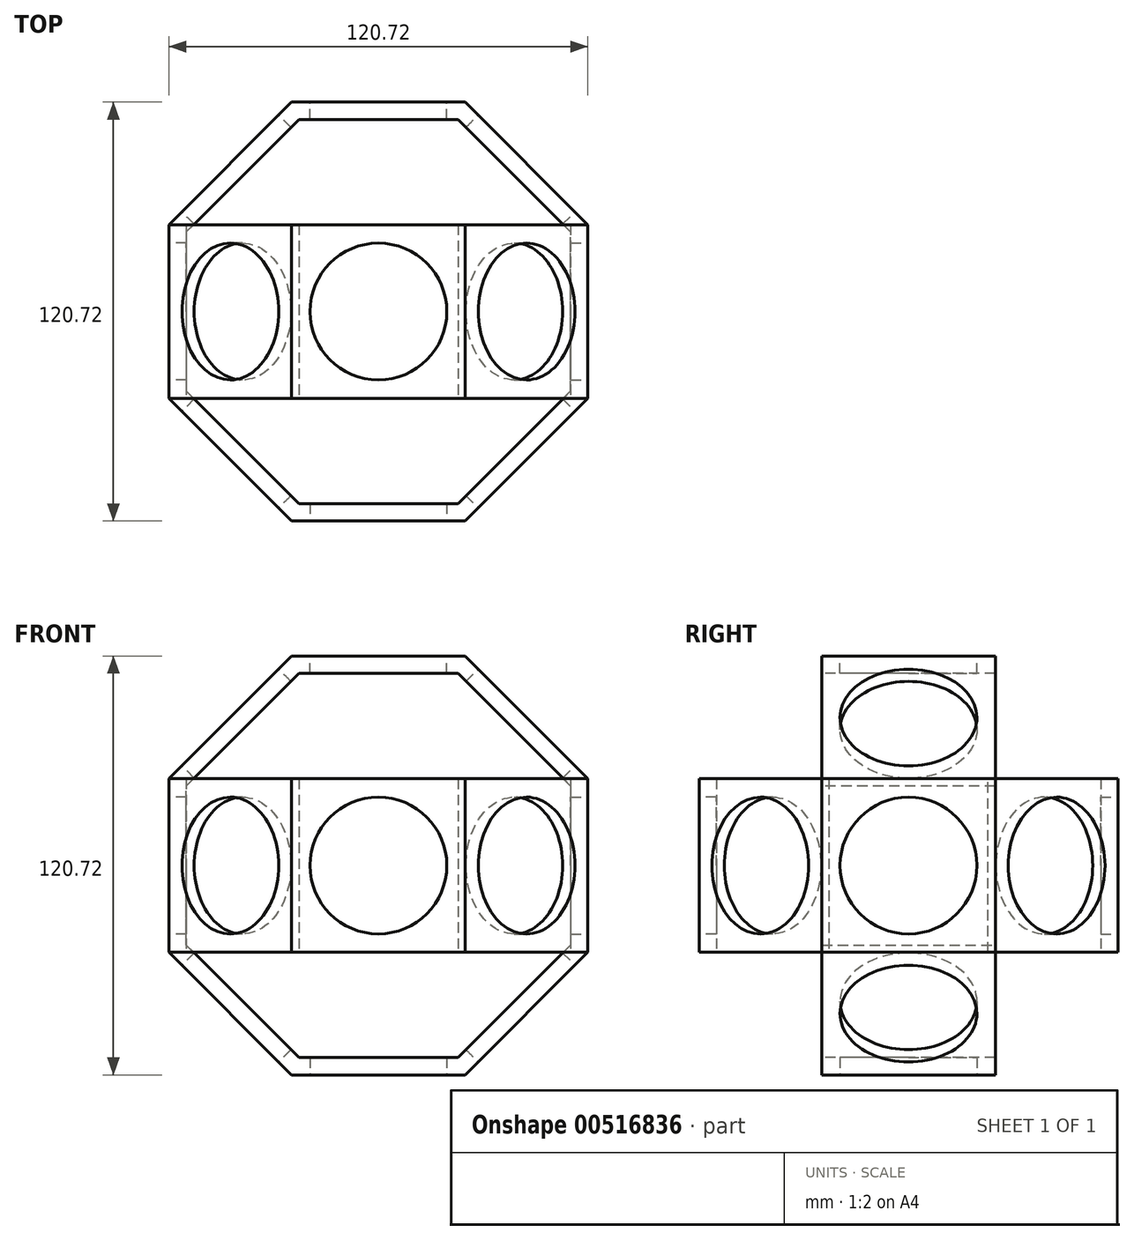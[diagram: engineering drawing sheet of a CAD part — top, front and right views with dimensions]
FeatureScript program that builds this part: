
annotation { "Feature Type Name" : "Feature", "Feature Type Description" : "" }
export const myFeature = defineFeature(function(context is Context, id is Id, definition is map)
    precondition{}
    {
        {
            var Q0;
            Q0=qCreatedBy(makeId("Top.planeOp"),FACE);
            var sketch = newSketch(context, id + "F0", { "sketchPlane" : qUnion([Q0])});
            skLineSegment(sketch, "E0", {"start": v(0, 0) * mm, "end": v(0, -20) * mm, "construction": true});
            skLineSegment(sketch, "E1", {"start": v(0, -20) * mm, "end": v(0, -25) * mm});
            skLineSegment(sketch, "E2", {"start": v(0, 0) * mm, "end": v(20, 0) * mm, "construction": true});
            skLineSegment(sketch, "E3", {"start": v(20, 0) * mm, "end": v(25, 0) * mm, "construction": true});
            skLineSegment(sketch, "E4", {"start": v(60.36, 0) * mm, "end": v(60.36, -25) * mm});
            skLineSegment(sketch, "E5", {"start": v(60.36, -25) * mm, "end": v(0, -25) * mm});
            skLineSegment(sketch, "E6", {"start": v(60.36, 25) * mm, "end": v(60.36, 0) * mm});
            skLineSegment(sketch, "E7", {"start": v(25, 0) * mm, "end": v(25, -60.36) * mm, "construction": true});
            skLineSegment(sketch, "E8", {"start": v(25, -60.36) * mm, "end": v(42.68, -42.68) * mm, "construction": true});
            skLineSegment(sketch, "E9", {"start": v(42.68, -42.68) * mm, "end": v(60.36, -25) * mm, "construction": true});
            skLineSegment(sketch, "E10", {"start": v(0, 0) * mm, "end": v(0, 20) * mm, "construction": true});
            skLineSegment(sketch, "E11", {"start": v(0, 20) * mm, "end": v(0, 25) * mm});
            skLineSegment(sketch, "E12", {"start": v(0, 25) * mm, "end": v(55.36, 25) * mm});
            skLineSegment(sketch, "E13", {"start": v(55.36, 25) * mm, "end": v(60.36, 25) * mm});
            skLineSegment(sketch, "E14", {"start": v(0, 20) * mm, "end": v(55.36, 20) * mm, "construction": true});
            skLineSegment(sketch, "E15", {"start": v(55.36, 20) * mm, "end": v(55.36, -20) * mm});
            skLineSegment(sketch, "E16", {"start": v(55.36, -20) * mm, "end": v(0, -20) * mm, "construction": true});
            skLineSegment(sketch, "E17", {"start": v(55.36, -20) * mm, "end": v(55.36, -25) * mm});
            skLineSegment(sketch, "E18", {"start": v(55.36, 20) * mm, "end": v(55.36, 25) * mm});
            skSolve(sketch);
        }
        {
            var Q0;
            {var subQ1=sQuery(id+"F0.wireOp",EDGE,"E4");Q0=makeQuery(id+"F0.imprint","IMPRINT",FACE,{"disambiguationData":[TD([[makeQuery(id+"F0.imprint","IMPRINT",EDGE,{"derivedFrom":subQ1}),-1.0]])]});}
            extrude(context, id + "F1", {"entities" : qUnion([Q0]), "depth" : 25 * mm, "offsetDistance" : 25 * mm, "hasSecondDirection" : true, "secondDirectionOppositeDirection" : true, "secondDirectionDepth" : 25 * mm});
        }
        {
            var Q0;
            Q0=makeQuery(id+"F1.opExtrude","SWEPT_FACE",FACE,{"disambiguationData":[OSD([sQuery(id+"F0.wireOp",EDGE,"E4"),sQuery(id+"F0.wireOp",EDGE,"E6")])]});
            var sketch = newSketch(context, id + "F2", { "sketchPlane" : qUnion([Q0])});
            skCircle(sketch, "E19", {"center": v(0, 0) * mm, "radius": 19.71 * mm});
            skSolve(sketch);
        }
        {
            var Q0;
            Q0=makeQuery(id+"F2.imprint","IMPRINT",FACE,{"disambiguationData":[TD([[makeQuery(id+"F2.imprint","IMPRINT",EDGE,{"derivedFrom":sQuery(id+"F2.wireOp",EDGE,"E19")}),1.0]])]});
            extrude(context, id + "F3", {"entities" : qUnion([Q0]), "operationType" : NewBodyOperationType.REMOVE, "oppositeDirection" : true, "depth" : 25 * mm, "offsetDistance" : 25 * mm});
        }
        {
            var Q0;
            Q0=makeQuery(id+"F1.opExtrude","SWEPT_BODY",BODY,{"disambiguationData":[OSD([sQuery(id+"F0.wireOp",EDGE,"E1"),sQuery(id+"F0.wireOp",EDGE,"E4"),sQuery(id+"F0.wireOp",EDGE,"E5"),sQuery(id+"F0.wireOp",EDGE,"E6"),sQuery(id+"F0.wireOp",EDGE,"E11"),sQuery(id+"F0.wireOp",EDGE,"E12"),sQuery(id+"F0.wireOp",EDGE,"E13"),sQuery(id+"F0.wireOp",EDGE,"E14"),sQuery(id+"F0.wireOp",EDGE,"E15"),sQuery(id+"F0.wireOp",EDGE,"E16")])]});
            var Q1;
            Q1=sQuery(id+"F0.wireOp",EDGE,"E0");
            circularPattern(context, id + "F4", {"operationType" : NewBodyOperationType.ADD, "entities" : qUnion([Q0]), "axis" : qUnion([Q1]), "angle" : 360 * degree, "instanceCount" : 8, "equalSpace" : true});
        }
        {
            var Q0;
            Q0=makeQuery(id+"F1.opExtrude","SWEPT_BODY",BODY,{"disambiguationData":[OSD([sQuery(id+"F0.wireOp",EDGE,"E1"),sQuery(id+"F0.wireOp",EDGE,"E4"),sQuery(id+"F0.wireOp",EDGE,"E5"),sQuery(id+"F0.wireOp",EDGE,"E6"),sQuery(id+"F0.wireOp",EDGE,"E11"),sQuery(id+"F0.wireOp",EDGE,"E12"),sQuery(id+"F0.wireOp",EDGE,"E13"),sQuery(id+"F0.wireOp",EDGE,"E14"),sQuery(id+"F0.wireOp",EDGE,"E15"),sQuery(id+"F0.wireOp",EDGE,"E16")])]});
            var Q1;
            Q1=sQuery(id+"F0.wireOp",EDGE,"E2");
            circularPattern(context, id + "F5", {"entities" : qUnion([Q0]), "axis" : qUnion([Q1]), "angle" : 90 * degree, "instanceCount" : 2, "equalSpace" : true});
        }
    });
